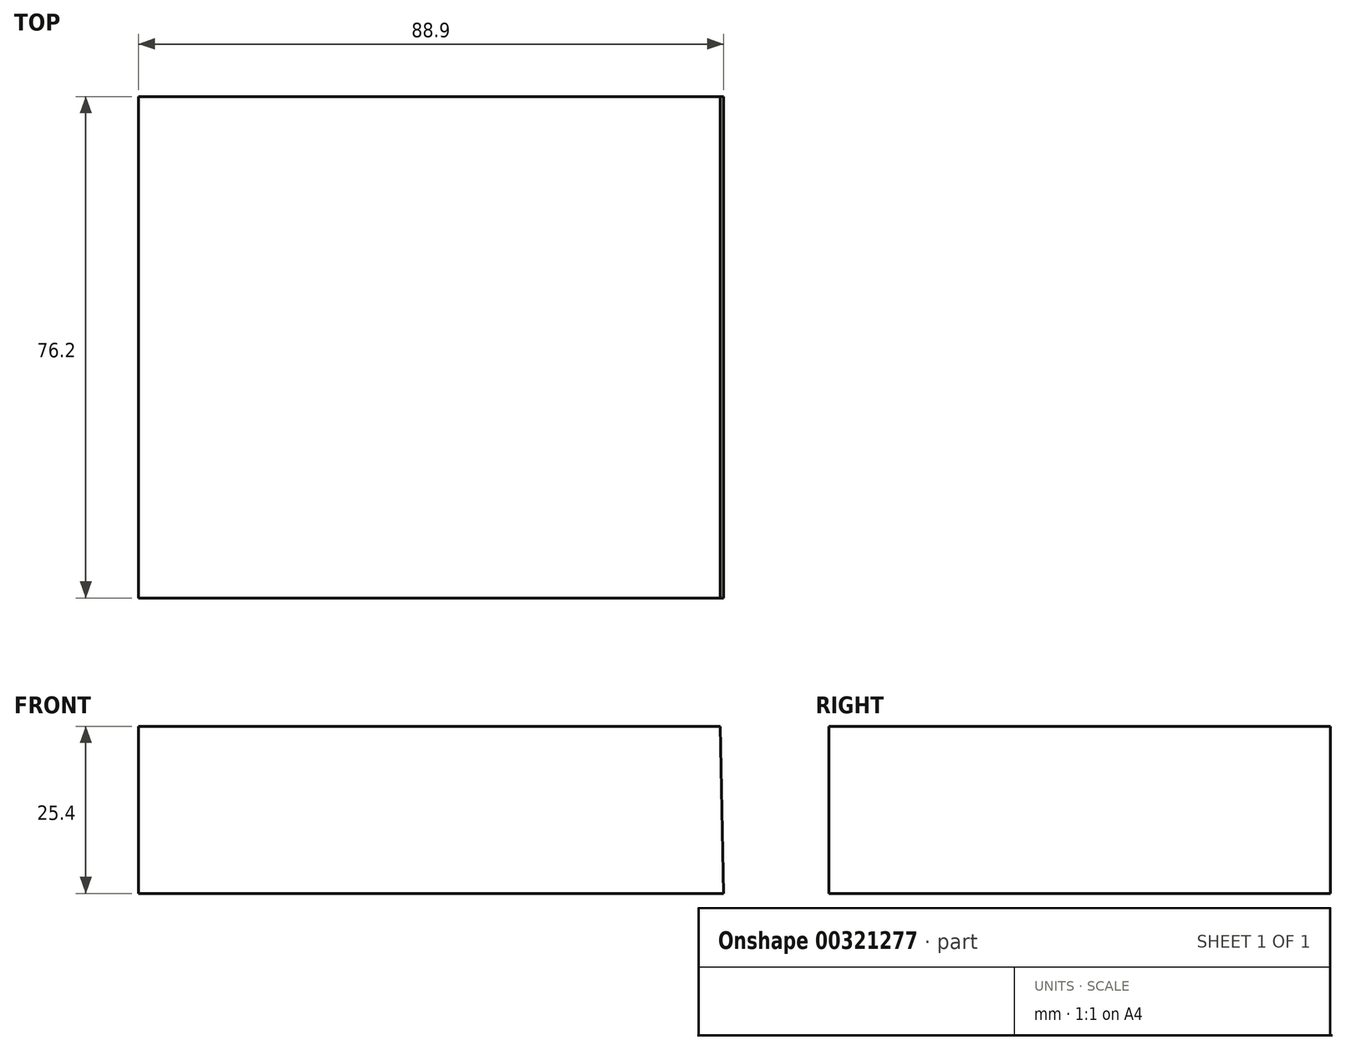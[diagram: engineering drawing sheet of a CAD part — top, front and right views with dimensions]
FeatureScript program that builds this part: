
annotation { "Feature Type Name" : "Feature", "Feature Type Description" : "" }
export const myFeature = defineFeature(function(context is Context, id is Id, definition is map)
    precondition{}
    {
        {
            var Q0;
            Q0=qCreatedBy(makeId("Front.planeOp"),FACE);
            var sketch = newSketch(context, id + "F0", { "sketchPlane" : qUnion([Q0])});
            skLineSegment(sketch, "E0", {"start": v(-49.01, -30.38) * mm, "end": v(39.89, -30.38) * mm});
            skLineSegment(sketch, "E1", {"start": v(-49.01, -30.38) * mm, "end": v(-49.01, -4.98) * mm});
            skLineSegment(sketch, "E2", {"start": v(-49.01, -4.98) * mm, "end": v(39.36, -4.98) * mm});
            skLineSegment(sketch, "E3", {"start": v(39.36, -4.98) * mm, "end": v(39.89, -30.38) * mm});
            skSolve(sketch);
        }
        {
            var Q0;
            Q0=makeQuery(id+"F0.imprint","IMPRINT",FACE,{"disambiguationData":[TD([[makeQuery(id+"F0.imprint","IMPRINT",EDGE,{"derivedFrom":sQuery(id+"F0.wireOp",EDGE,"E0")}),1.0]])]});
            extrude(context, id + "F1", {"entities" : qUnion([Q0]), "oppositeDirection" : true, "depth" : 76.2 * mm});
        }
    });
